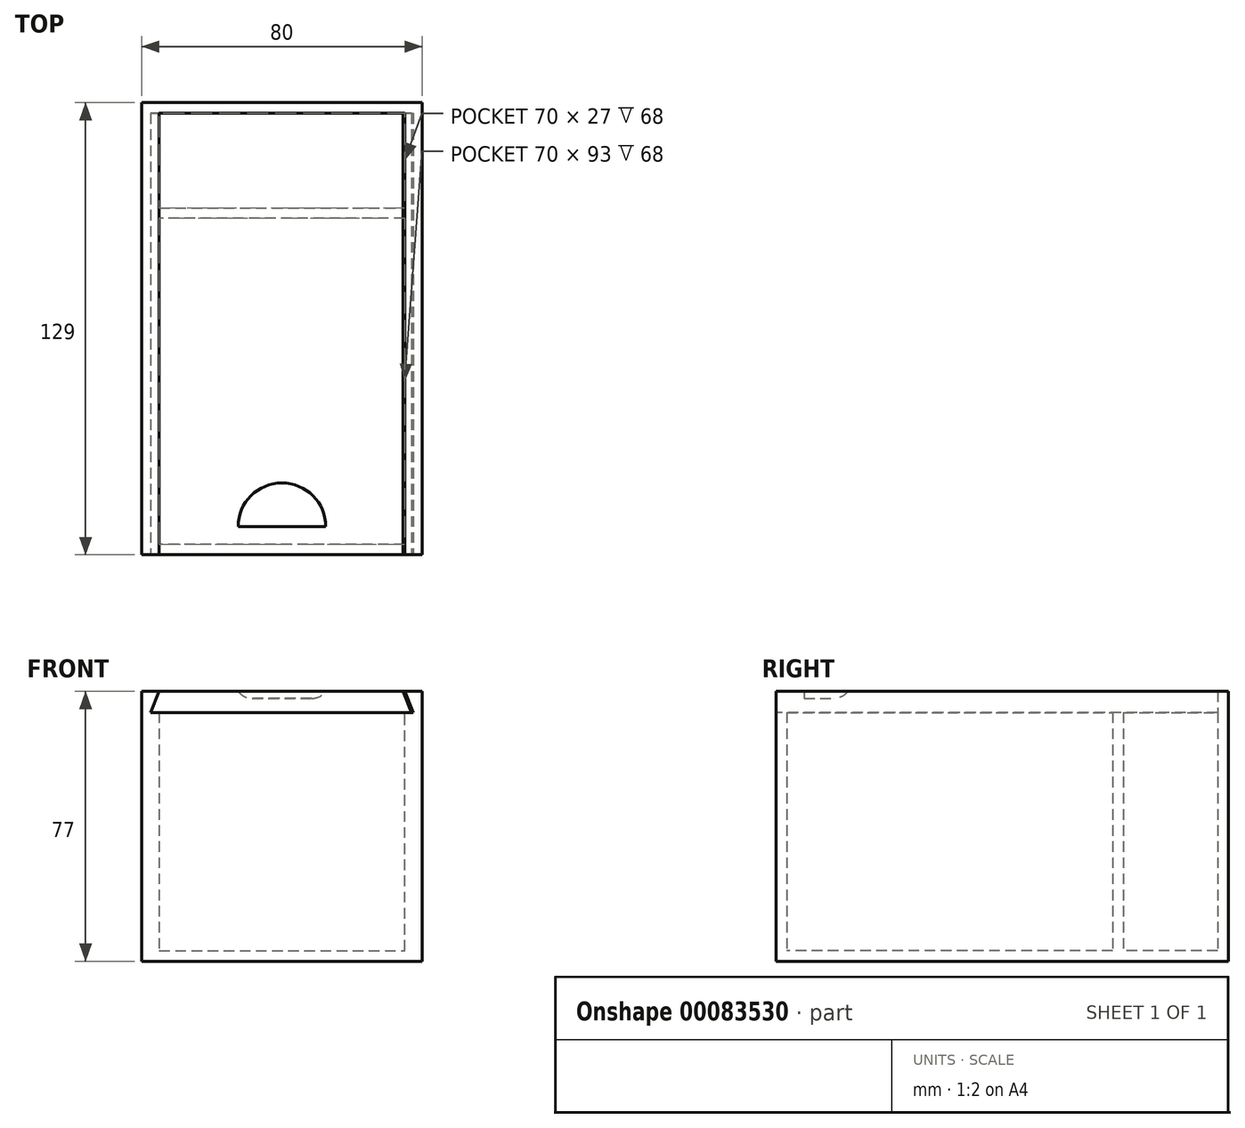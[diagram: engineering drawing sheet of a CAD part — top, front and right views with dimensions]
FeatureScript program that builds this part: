
annotation { "Feature Type Name" : "Feature", "Feature Type Description" : "" }
export const myFeature = defineFeature(function(context is Context, id is Id, definition is map)
    precondition{}
    {
        {
            var Q0;
            Q0=qCreatedBy(makeId("Top.planeOp"),FACE);
            var sketch = newSketch(context, id + "F0", { "sketchPlane" : qUnion([Q0])});
            skLineSegment(sketch, "E0.bottom", {"start": v(0, 0) * mm, "end": v(70, 0) * mm});
            skLineSegment(sketch, "E0.top", {"start": v(0, -93) * mm, "end": v(70, -93) * mm});
            skLineSegment(sketch, "E0.left", {"start": v(0, 0) * mm, "end": v(0, -93) * mm});
            skLineSegment(sketch, "E0.right", {"start": v(70, 0) * mm, "end": v(70, -93) * mm});
            skLineSegment(sketch, "E1.0", {"start": v(-3, 3) * mm, "end": v(73, 3) * mm});
            skLineSegment(sketch, "E1.1", {"start": v(-3, 3) * mm, "end": v(-3, -96) * mm});
            skLineSegment(sketch, "E1.2", {"start": v(-3, -96) * mm, "end": v(73, -96) * mm});
            skLineSegment(sketch, "E1.3", {"start": v(73, 3) * mm, "end": v(73, -96) * mm});
            skSolve(sketch);
        }
        {
            var Q0;
            Q0=makeQuery(id+"F0.imprint","IMPRINT",FACE,{"disambiguationData":[TD([[makeQuery(id+"F0.imprint","IMPRINT",EDGE,{"derivedFrom":sQuery(id+"F0.wireOp",EDGE,"E0.bottom")}),1.0]])]});
            var Q1;
            Q1=makeQuery(id+"F0.imprint","IMPRINT",FACE,{"disambiguationData":[TD([[makeQuery(id+"F0.imprint","IMPRINT",EDGE,{"derivedFrom":sQuery(id+"F0.wireOp",EDGE,"E0.bottom")}),-1.0]])]});
            extrude(context, id + "F1", {"entities" : qUnion([Q0, Q1]), "depth" : 77 * mm});
        }
        {
            var Q0;
            Q0=makeQuery(id+"F1.opExtrude","CAP_FACE",FACE,{"disambiguationData":[OSD([sQuery(id+"F0.wireOp",EDGE,"E1.0"),sQuery(id+"F0.wireOp",EDGE,"E1.1"),sQuery(id+"F0.wireOp",EDGE,"E1.2"),sQuery(id+"F0.wireOp",EDGE,"E1.3")])],"isStart":false});
            shell(context, id + "F2", {"entities" : qUnion([Q0]), "thickness" : 3 * mm});
        }
        {
            var Q0;
            Q0=makeQuery(id+"F1.opExtrude","SWEPT_FACE",FACE,{"disambiguationData":[OSD([sQuery(id+"F0.wireOp",EDGE,"E1.0")])]});
            extrude(context, id + "F3", {"entities" : qUnion([Q0]), "operationType" : NewBodyOperationType.ADD, "depth" : 30 * mm});
        }
        {
            var Q0;
            {var subQ0=sQuery(id+"F0.wireOp",EDGE,"E1.0");Q0=makeQuery(id+"F3.boolean.opBoolean","MERGE",FACE,{"derivedFrom":[makeQuery(id+"F1.opExtrude","CAP_FACE",FACE,{"disambiguationData":[OSD([subQ0,sQuery(id+"F0.wireOp",EDGE,"E1.1"),sQuery(id+"F0.wireOp",EDGE,"E1.2"),sQuery(id+"F0.wireOp",EDGE,"E1.3")])],"isStart":false}),makeQuery(id+"F3.opExtrude","SWEPT_FACE",FACE,{"disambiguationData":[OSD([subQ0]),TDD([makeQuery(id+"F1.opExtrude","CAP_EDGE",EDGE,{"disambiguationData":[OSD([subQ0])],"isStart":false})])]})]});}
            shell(context, id + "F4", {"entities" : qUnion([Q0]), "thickness" : 3 * mm});
        }
        {
            var Q0;
            {var subQ0=sQuery(id+"F0.wireOp",EDGE,"E1.1");Q0=makeQuery(id+"F3.boolean.opBoolean","MERGE",FACE,{"derivedFrom":[makeQuery(id+"F1.opExtrude","SWEPT_FACE",FACE,{"disambiguationData":[OSD([subQ0])]}),makeQuery(id+"F3.opExtrude","SWEPT_FACE",FACE,{"disambiguationData":[OSD([sQuery(id+"F0.wireOp",EDGE,"E1.0"),subQ0])]})]});}
            extrude(context, id + "F5", {"entities" : qUnion([Q0]), "operationType" : NewBodyOperationType.ADD, "depth" : 2 * mm});
        }
        {
            var Q0;
            {var subQ0=sQuery(id+"F0.wireOp",EDGE,"E1.3");Q0=makeQuery(id+"F3.boolean.opBoolean","MERGE",FACE,{"derivedFrom":[makeQuery(id+"F1.opExtrude","SWEPT_FACE",FACE,{"disambiguationData":[OSD([subQ0])]}),makeQuery(id+"F3.opExtrude","SWEPT_FACE",FACE,{"disambiguationData":[OSD([sQuery(id+"F0.wireOp",EDGE,"E1.0"),subQ0])]})]});}
            extrude(context, id + "F6", {"entities" : qUnion([Q0]), "operationType" : NewBodyOperationType.ADD, "depth" : 2 * mm});
        }
        {
            var Q0;
            {var subQ0=sQuery(id+"F0.wireOp",EDGE,"E1.2");Q0=makeQuery(id+"F6.boolean.opBoolean","MERGE",FACE,{"derivedFrom":[makeQuery(id+"F5.boolean.opBoolean","MERGE",FACE,{"derivedFrom":[makeQuery(id+"F1.opExtrude","SWEPT_FACE",FACE,{"disambiguationData":[OSD([subQ0])]}),makeQuery(id+"F5.opExtrude","SWEPT_FACE",FACE,{"disambiguationData":[OSD([sQuery(id+"F0.wireOp",EDGE,"E1.1"),subQ0])]})]}),makeQuery(id+"F6.opExtrude","SWEPT_FACE",FACE,{"disambiguationData":[OSD([subQ0,sQuery(id+"F0.wireOp",EDGE,"E1.3")])]})]});}
            var sketch = newSketch(context, id + "F7", { "sketchPlane" : qUnion([Q0])});
            skLineSegment(sketch, "E2", {"start": v(0, 77) * mm, "end": v(0, 0) * mm, "construction": true});
            skLineSegment(sketch, "E3", {"start": v(70, 77) * mm, "end": v(70, 0) * mm, "construction": true});
            skLineSegment(sketch, "E4", {"start": v(-5, 71) * mm, "end": v(75, 71) * mm, "construction": true});
            skLineSegment(sketch, "E5", {"start": v(72.5, 77) * mm, "end": v(72.5, 0) * mm, "construction": true});
            skLineSegment(sketch, "E6", {"start": v(-2.5, 77) * mm, "end": v(-2.5, 0) * mm, "construction": true});
            skLineSegment(sketch, "E7", {"start": v(0, 77) * mm, "end": v(-2.5, 71) * mm});
            skLineSegment(sketch, "E8", {"start": v(-2.5, 71) * mm, "end": v(72.5, 71) * mm});
            skLineSegment(sketch, "E9", {"start": v(72.5, 71) * mm, "end": v(70, 77) * mm});
            skSolve(sketch);
        }
        {
            var Q0;
            {var subQ0=sQuery(id+"F7.wireOp",EDGE,"E7");Q0=makeQuery(id+"F7.imprint","IMPRINT",FACE,{"disambiguationData":[TD([[makeQuery(id+"F7.imprint","IMPRINT",EDGE,{"derivedFrom":subQ0}),1.0]])]});}
            var Q1;
            {var subQ0=sQuery(id+"F0.wireOp",EDGE,"E1.0");Q1=makeQuery(id+"F4.opShell","OFFSET_FACE",FACE,{"disambiguationData":[OSD([subQ0]),TDD([makeQuery(id+"F3.opExtrude","CAP_FACE",FACE,{"disambiguationData":[OSD([subQ0])],"isStart":false})])]});}
            extrude(context, id + "F8", {"entities" : qUnion([Q0]), "operationType" : NewBodyOperationType.REMOVE, "endBound" : BoundingType.UP_TO_SURFACE, "oppositeDirection" : true, "endBoundEntityFace" : qUnion([Q1]), "depth" : 25 * mm});
        }
        {
            var Q0;
            {var subQ0=sQuery(id+"F0.wireOp",EDGE,"E1.2");Q0=makeQuery(id+"F6.boolean.opBoolean","MERGE",FACE,{"derivedFrom":[makeQuery(id+"F5.boolean.opBoolean","MERGE",FACE,{"derivedFrom":[makeQuery(id+"F1.opExtrude","SWEPT_FACE",FACE,{"disambiguationData":[OSD([subQ0])]}),makeQuery(id+"F5.opExtrude","SWEPT_FACE",FACE,{"disambiguationData":[OSD([sQuery(id+"F0.wireOp",EDGE,"E1.1"),subQ0])]})]}),makeQuery(id+"F6.opExtrude","SWEPT_FACE",FACE,{"disambiguationData":[OSD([subQ0,sQuery(id+"F0.wireOp",EDGE,"E1.3")])]})]});}
            var sketch = newSketch(context, id + "F9", { "sketchPlane" : qUnion([Q0])});
            skLineSegment(sketch, "E10.0", {"start": v(0, 77) * mm, "end": v(70, 77) * mm});
            skLineSegment(sketch, "E10.1", {"start": v(0, 77) * mm, "end": v(-2.5, 71) * mm});
            skLineSegment(sketch, "E10.2", {"start": v(-2.5, 71) * mm, "end": v(72.5, 71) * mm});
            skLineSegment(sketch, "E10.3", {"start": v(72.5, 71) * mm, "end": v(70, 77) * mm});
            skLineSegment(sketch, "E11", {"start": v(72, 71) * mm, "end": v(69.5, 77) * mm});
            skSolve(sketch);
        }
        {
            var Q0;
            {var subQ0=sQuery(id+"F9.wireOp",EDGE,"E10.1");Q0=makeQuery(id+"F9.imprint","IMPRINT",FACE,{"disambiguationData":[TD([[makeQuery(id+"F9.imprint","IMPRINT",EDGE,{"derivedFrom":subQ0}),1.0]])]});}
            var Q1;
            {var subQ0=sQuery(id+"F0.wireOp",EDGE,"E1.0");Q1=makeQuery(id+"F8.boolean.opBoolean","MERGE",FACE,{"derivedFrom":[makeQuery(id+"F4.opShell","OFFSET_FACE",FACE,{"disambiguationData":[OSD([subQ0]),TDD([makeQuery(id+"F3.opExtrude","CAP_FACE",FACE,{"disambiguationData":[OSD([subQ0])],"isStart":false})])]}),makeQuery(id+"F8.opExtrude","CAP_FACE",FACE,{"disambiguationData":[OSD([sQuery(id+"F0.wireOp",EDGE,"E1.1"),sQuery(id+"F0.wireOp",EDGE,"E1.2"),sQuery(id+"F0.wireOp",EDGE,"E1.3"),sQuery(id+"F7.wireOp",EDGE,"E7"),sQuery(id+"F7.wireOp",EDGE,"E8"),sQuery(id+"F7.wireOp",EDGE,"E9")])],"isStart":false})]});}
            extrude(context, id + "F10", {"entities" : qUnion([Q0]), "endBound" : BoundingType.UP_TO_SURFACE, "oppositeDirection" : true, "endBoundEntityFace" : qUnion([Q1]), "depth" : (93 + 3) * mm});
        }
        {
            var Q0;
            Q0=makeQuery(id+"F10.opExtrude","SWEPT_FACE",FACE,{"disambiguationData":[OSD([sQuery(id+"F9.wireOp",EDGE,"E10.0")])]});
            var sketch = newSketch(context, id + "F11", { "sketchPlane" : qUnion([Q0])});
            skLineSegment(sketch, "E12", {"start": v(0, -88) * mm, "end": v(0, -88) * mm});
            skArc(sketch, "E13", {"start": v(47.5, -88) * mm, "mid": v(35, -75.5) * mm, "end": v(22.5, -88) * mm});
            skLineSegment(sketch, "E14", {"start": v(22.5, -88) * mm, "end": v(47.5, -88) * mm});
            skSolve(sketch);
        }
        {
            var Q0;
            Q0=makeQuery(id+"F11.imprint","IMPRINT",FACE,{"disambiguationData":[TD([[makeQuery(id+"F11.imprint","IMPRINT",EDGE,{"derivedFrom":sQuery(id+"F11.wireOp",EDGE,"E13")}),1.0]])]});
            extrude(context, id + "F12", {"entities" : qUnion([Q0]), "operationType" : NewBodyOperationType.REMOVE, "oppositeDirection" : true, "depth" : 2 * mm});
        }
        {
            var Q0;
            Q0=makeQuery(id+"F12.boolean.opBoolean","COPY",EDGE,{"derivedFrom":makeQuery(id+"F12.opExtrude","CAP_EDGE",EDGE,{"disambiguationData":[OSD([sQuery(id+"F11.wireOp",EDGE,"E13")])],"isStart":false})});
            fillet(context, id + "F13", {"entities" : qUnion([Q0]), "radius" : 5 * mm, "tangentPropagation" : true, "allowEdgeOverflow" : false});
        }
    });
